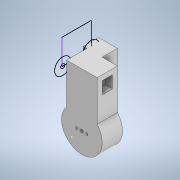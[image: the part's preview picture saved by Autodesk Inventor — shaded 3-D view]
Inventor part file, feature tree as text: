
AUTODESK INVENTOR PART (.ipt)
format: ipt  version: 2022 (Build 260153000, 153)  size: 351,232 bytes
history: native  units: in
note: dims shown in document units (in); Inventor stores cm internally (conversion verified against a paired STEP export)
features: sketch x37, extrude x26, chamfer x1
ambient origin geometry x8: Origin, YZ Plane, XZ Plane, XY Plane, X Axis, Y Axis, Z Axis, Center Point
bodies: Solid1 (feature_tree)
feature tree (64):
  extrude  "Extrusion1"  Depth=0.7874in
  extrude  "Extrusion2"  Depth=1.1811in
  extrude  "Extrusion3"  Depth=0.7874in
  extrude  "Extrusion4"  Depth=0.2362in
  extrude  "Extrusion5"  Depth=0.2362in
  extrude  "Extrusion6"  Depth=0.9055in TaperAngle=0.0deg
  extrude  "Extrusion7"  Depth=0.189in
  extrude  "Extrusion8"  Depth=0.6299in TaperAngle=0.0deg
  sketch  "Sketch11"  dims[d24=0.0984in d25=0.0591in]
  extrude  "Extrusion9"  Depth=0.0591in
  extrude  "Extrusion10"  Depth=0.0591in
  extrude  "Extrusion11"  Depth=0.3937in
  extrude  "Extrusion12"  Depth=0.1969in
  extrude  "Extrusion13"  Depth=0.1969in TaperAngle=0.0deg
  extrude  "Extrusion15"  Depth=0.1181in
  extrude  "Extrusion16"  Depth=0.1181in
  extrude  "Extrusion17"  Depth=0.3937in TaperAngle=0.0deg
  extrude  "Extrusion18"  Depth=0.3937in
  chamfer  "Chamfer2"  Distance=2.3469in
  sketch  "Sketch22"  dims[d51=0.3937in d52=0.0in d53=0.3937in d54=0.0in]
  sketch  "Sketch25"  dims[d56=0.9843in d57=0.3937in d58=0.0in]
  sketch  "Sketch29"  dims[d59=0.3937in d60=0.0in d70=0.6299in d71=0.0in]
  extrude  "Extrusion27"  Depth=0.3937in TaperAngle=0.0deg
  sketch  "Sketch34"  dims[d75=1.1826in d76=0.0in d77=0.0787in]
  sketch  "Sketch37"  dims[d78=0.0787in d79=5.4424in d80=0.0in]
  sketch  "Sketch38"  dims[d81=0.315in d82=0.0787in d83=45.0deg d92=0.6299in]
  extrude  "Extrusion31"  Depth=0.3937in TaperAngle=0.0deg
  extrude  "Extrusion32"  Depth=0.6299in TaperAngle=0.0deg
  extrude  "Extrusion33"  Depth=0.6299in TaperAngle=0.0deg
  extrude  "Extrusion34"  Depth=0.0787in
  extrude  "Extrusion35"  Depth=5.4424in TaperAngle=0.0deg
  sketch  "Sketch46"  dims[d124=0.1969in d125=0.0in]
  sketch  "Sketch47"  dims[d126=0.3937in d127=0.0in]
  extrude  "Extrusion36"  Depth=0.6299in
  extrude  "Extrusion37"  Depth=0.6299in
  sketch  "Sketch50"  dims[d130=0.6299in]
  sketch  "Sketch51"  dims[d131=0.1969in]
  sketch  "Sketch52"  dims[d132=0.2362in d133=0.0in]
  extrude  "Extrusion38"  Depth=0.3937in
  sketch  "Sketch1"  dims[d0=0.7874in d1=1.5748in]
  sketch  "Sketch2"  dims[d2=1.1811in d3=1.9685in]
  sketch  "Sketch4"  dims[d4=0.7874in d5=0.0in d6=0.7874in]
  sketch  "Sketch6"  dims[d7=0.5906in d8=0.0in d13=0.2362in]
  sketch  "Sketch7"  dims[d14=0.9843in d15=0.2362in]
  sketch  "Sketch8"  dims[d16=0.9055in d17=0.9055in d18=0.0in]
  sketch  "Sketch9"  dims[d19=0.4724in d20=0.189in]
  sketch  "Sketch10"  dims[d21=0.189in d22=0.6299in d23=0.0in]
  sketch  "Sketch12"  dims[d26=0.0984in d27=0.0591in]
  sketch  "Sketch13"  dims[d28=0.315in d29=0.0in d30=0.3937in]
  sketch  "Sketch15"  dims[d31=0.315in d32=0.1969in]
  sketch  "Sketch16"  dims[d33=0.1969in d34=0.6225in d35=0.0in]
  sketch  "Sketch18"  dims[d36=0.0787in d37=0.1181in]
  sketch  "Sketch19"  dims[d38=0.1181in d39=0.1181in]
  sketch  "Sketch20"  dims[d40=0.315in d41=0.0in d45=0.3937in d46=0.0in]
  sketch  "Sketch21"  dims[d47=0.5906in d48=0.3937in d49=2.3469in d50=0.0in]
  sketch  "Sketch33"  dims[d72=0.7874in d73=0.6299in d74=0.0in]
  sketch  "Sketch41"  dims[d93=0.6299in d94=0.6299in]
  sketch  "Sketch42"  dims[d99=0.9843in d110=0.3937in]
  sketch  "Sketch43"  dims[d111=0.315in]
  sketch  "Sketch44"  dims[d112=0.2756in d113=0.0in]
  sketch  "Sketch45"  dims[d122=1.4188in d123=0.0in]
  sketch  "Sketch48"  dims[d128=0.6299in]
  sketch  "Sketch49"  dims[d129=0.7087in]
  sketch  "Sketch53"  dims[d134=0.2756in d135=0.0in d136=0.2362in d137=0.0in d138=0.1417in d139=0.0in d140=0.1772in d141=0.3307in d142=0.0in]
